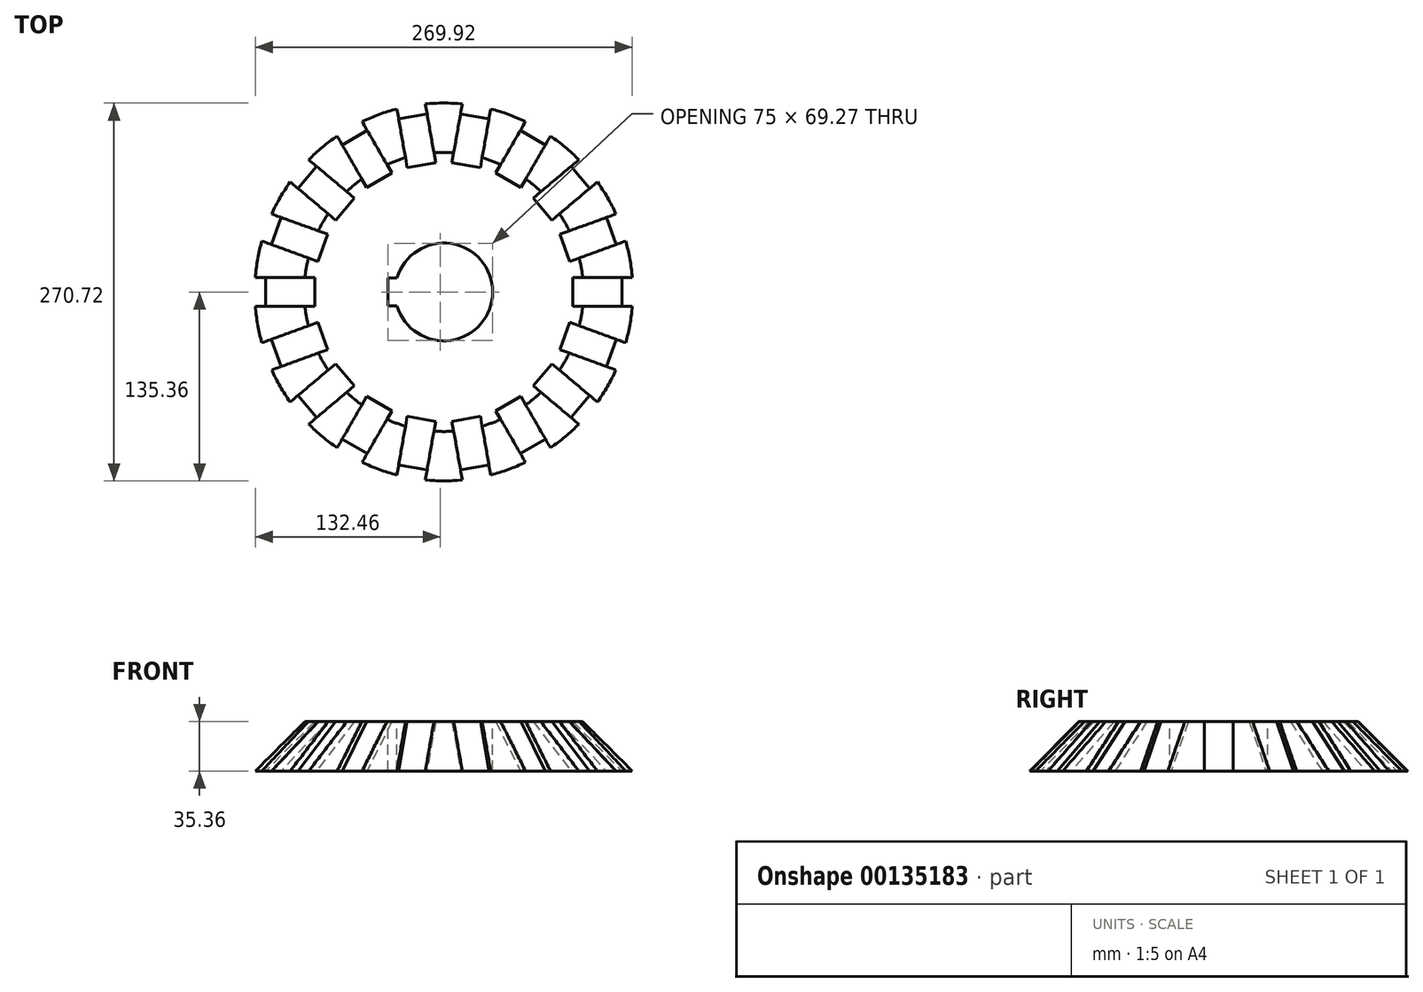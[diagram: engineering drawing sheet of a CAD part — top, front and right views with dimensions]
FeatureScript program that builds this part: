
annotation { "Feature Type Name" : "Feature", "Feature Type Description" : "" }
export const myFeature = defineFeature(function(context is Context, id is Id, definition is map)
    precondition{}
    {
        {
            var Q0;
            Q0=qCreatedBy(makeId("Front.planeOp"),FACE);
            var sketch = newSketch(context, id + "F0", { "sketchPlane" : qUnion([Q0])});
            skLineSegment(sketch, "E0", {"start": v(0, 0) * mm, "end": v(-100, 0) * mm});
            skLineSegment(sketch, "E1", {"start": v(-100, 0) * mm, "end": v(-135.36, -35.36) * mm});
            skLineSegment(sketch, "E2", {"start": v(-135.36, -35.36) * mm, "end": v(0, -35.36) * mm});
            skLineSegment(sketch, "E3", {"start": v(0, 0) * mm, "end": v(0, -35.36) * mm});
            skSolve(sketch);
        }
        {
            var Q0;
            Q0=makeQuery(id+"F0.imprint","IMPRINT",FACE,{"disambiguationData":[TD([[makeQuery(id+"F0.imprint","IMPRINT",EDGE,{"derivedFrom":sQuery(id+"F0.wireOp",EDGE,"E0")}),1.0]])]});
            var Q1;
            Q1=sQuery(id+"F0.wireOp",EDGE,"E3");
            revolve(context, id + "F1", {"entities" : qUnion([Q0]), "axis" : qUnion([Q1]), "revolveType" : RevolveType.FULL});
        }
        {
            var Q0;
            Q0=makeQuery(id+"F1.opRevolve","SWEPT_FACE",FACE,{"disambiguationData":[OSD([sQuery(id+"F0.wireOp",EDGE,"E0")])]});
            var sketch = newSketch(context, id + "F2", { "sketchPlane" : qUnion([Q0])});
            skCircle(sketch, "E4.0", {"center": v(0, 0) * mm, "radius": 100 * mm});
            skLineSegment(sketch, "E5.bottom", {"start": v(92.34, 10.34) * mm, "end": v(107.66, 10.34) * mm});
            skLineSegment(sketch, "E5.top", {"start": v(92.34, -10.34) * mm, "end": v(107.66, -10.34) * mm});
            skLineSegment(sketch, "E5.left", {"start": v(92.34, 10.34) * mm, "end": v(92.34, -10.34) * mm});
            skLineSegment(sketch, "E5.right", {"start": v(107.66, 10.34) * mm, "end": v(107.66, -10.34) * mm});
            skPoint(sketch, "E5.middle", {"position": v(100, 0) * mm});
            skSolve(sketch);
        }
        {
            var Q0;
            Q0=qCreatedBy(makeId("Front.planeOp"),FACE);
            var sketch = newSketch(context, id + "F3", { "sketchPlane" : qUnion([Q0])});
            skLineSegment(sketch, "E6", {"start": v(100, 0) * mm, "end": v(135.36, -35.36) * mm});
            skSolve(sketch);
        }
        {
            var Q0;
            {var subQ5=sQuery(id+"F2.wireOp",EDGE,"E5.left");Q0=makeQuery(id+"F2.imprint","IMPRINT",FACE,{"disambiguationData":[TD([[makeQuery(id+"F2.imprint","IMPRINT",EDGE,{"derivedFrom":subQ5}),1.0]])]});}
            var Q1;
            {var subQ5=sQuery(id+"F2.wireOp",EDGE,"E5.right");Q1=makeQuery(id+"F2.imprint","IMPRINT",FACE,{"disambiguationData":[TD([[makeQuery(id+"F2.imprint","IMPRINT",EDGE,{"derivedFrom":subQ5}),-1.0]])]});}
            var Q2;
            Q2=sQuery(id+"F3.wireOp",EDGE,"E6");
            sweep(context, id + "F4", {"profiles" : qUnion([Q0, Q1]), "path" : qUnion([Q2])});
        }
        {
            var Q0;
            Q0=qCreatedBy(makeId("Front.planeOp"),FACE);
            var sketch = newSketch(context, id + "F5", { "sketchPlane" : qUnion([Q0])});
            skLineSegment(sketch, "E7", {"start": v(0, 68.88) * mm, "end": v(0, -88.9) * mm});
            skSolve(sketch);
        }
        {
            var Q0;
            Q0=makeQuery(id+"F4.opSweep","SWEPT_BODY",BODY,{"disambiguationData":[OSD([sQuery(id+"F2.wireOp",EDGE,"E5.bottom"),sQuery(id+"F2.wireOp",EDGE,"E5.top"),sQuery(id+"F2.wireOp",EDGE,"E5.left"),sQuery(id+"F2.wireOp",EDGE,"E5.right"),sQuery(id+"F3.wireOp",EDGE,"E6")])]});
            var Q1;
            Q1=sQuery(id+"F5.wireOp",EDGE,"E7");
            circularPattern(context, id + "F6", {"operationType" : NewBodyOperationType.REMOVE, "entities" : qUnion([Q0]), "axis" : qUnion([Q1]), "angle" : 360 * degree, "instanceCount" : 18, "equalSpace" : true});
        }
        {
            var Q0;
            Q0=makeQuery(id+"F1.opRevolve","SWEPT_FACE",FACE,{"disambiguationData":[OSD([sQuery(id+"F0.wireOp",EDGE,"E0")])]});
            var sketch = newSketch(context, id + "F7", { "sketchPlane" : qUnion([Q0])});
            skArc(sketch, "E8", {"start": v(-33.54, -10) * mm, "mid": v(35, 0) * mm, "end": v(-33.54, 10) * mm});
            skLineSegment(sketch, "E9.bottom", {"start": v(-40, -10) * mm, "end": v(-33.54, -10) * mm});
            skLineSegment(sketch, "E9.top", {"start": v(-40, 10) * mm, "end": v(-33.54, 10) * mm});
            skLineSegment(sketch, "E9.left", {"start": v(-40, -10) * mm, "end": v(-40, 10) * mm});
            skPoint(sketch, "E9.middle", {"position": v(-35, 0) * mm});
            skSolve(sketch);
        }
        {
            var Q0;
            Q0=makeQuery(id+"F7.imprint","IMPRINT",FACE,{"disambiguationData":[TD([[makeQuery(id+"F7.imprint","IMPRINT",EDGE,{"derivedFrom":sQuery(id+"F7.wireOp",EDGE,"E8")}),1.0]])]});
            extrude(context, id + "F8", {"entities" : qUnion([Q0]), "operationType" : NewBodyOperationType.REMOVE, "oppositeDirection" : true, "depth" : 50 * mm});
        }
    });
